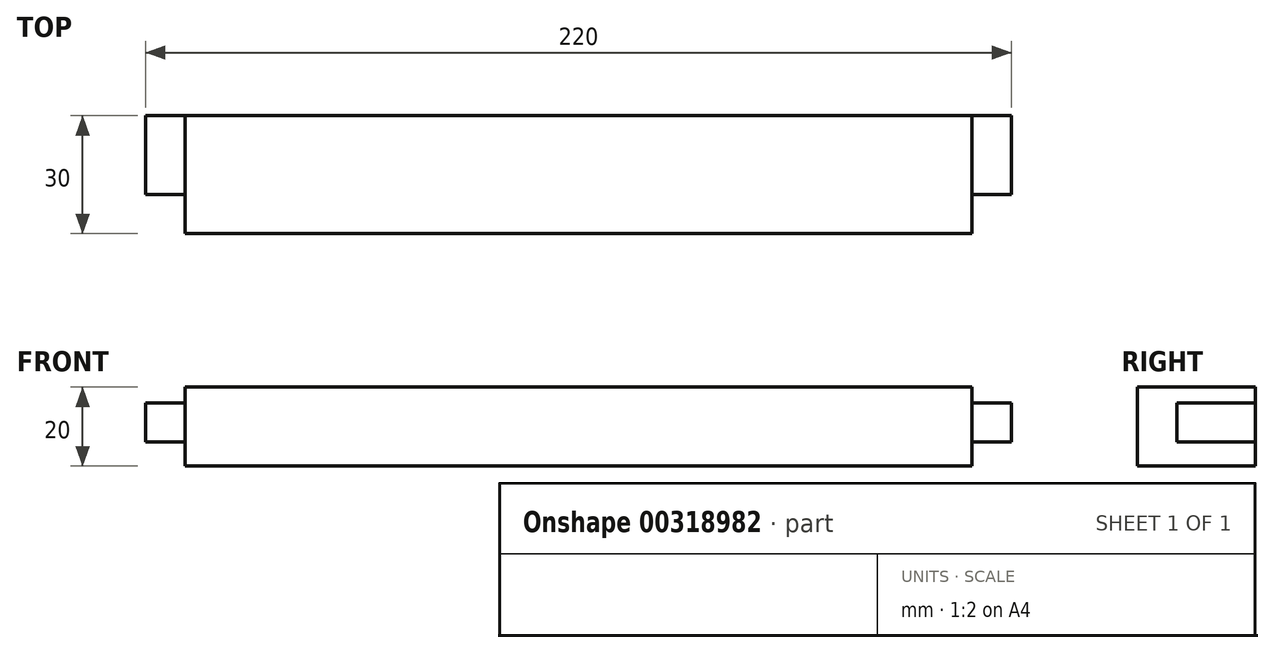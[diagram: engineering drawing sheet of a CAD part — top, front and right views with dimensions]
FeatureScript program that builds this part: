
annotation { "Feature Type Name" : "Feature", "Feature Type Description" : "" }
export const myFeature = defineFeature(function(context is Context, id is Id, definition is map)
    precondition{}
    {
        {
            var Q0;
            Q0=qCreatedBy(makeId("Top.planeOp"),FACE);
            var sketch = newSketch(context, id + "F0", { "sketchPlane" : qUnion([Q0])});
            skLineSegment(sketch, "E0.bottom", {"start": v(100, 15) * mm, "end": v(-100, 15) * mm});
            skLineSegment(sketch, "E0.top", {"start": v(100, -15) * mm, "end": v(-100, -15) * mm});
            skLineSegment(sketch, "E0.left", {"start": v(100, 15) * mm, "end": v(100, -15) * mm});
            skLineSegment(sketch, "E0.right", {"start": v(-100, 15) * mm, "end": v(-100, -15) * mm});
            skPoint(sketch, "E0.middle", {"position": v(0, 0) * mm});
            skSolve(sketch);
        }
        {
            var Q0;
            Q0=qSketchRegion(id+"F0",true);
            extrude(context, id + "F1", {"entities" : qUnion([Q0]), "depth" : 20 * mm});
        }
        {
            var Q0;
            Q0=makeQuery(id+"F1.opExtrude","SWEPT_FACE",FACE,{"disambiguationData":[OSD([sQuery(id+"F0.wireOp",EDGE,"E0.left")])]});
            var sketch = newSketch(context, id + "F2", { "sketchPlane" : qUnion([Q0])});
            skLineSegment(sketch, "E1", {"start": v(-5, 16.05) * mm, "end": v(-8.06, 20) * mm, "construction": true});
            skLineSegment(sketch, "E2.bottom", {"start": v(-5, 16.05) * mm, "end": v(15, 16.05) * mm});
            skLineSegment(sketch, "E2.top", {"start": v(-5, 6.05) * mm, "end": v(15, 6.05) * mm});
            skLineSegment(sketch, "E2.left", {"start": v(-5, 16.05) * mm, "end": v(-5, 6.05) * mm});
            skLineSegment(sketch, "E2.right", {"start": v(15, 16.05) * mm, "end": v(15, 6.05) * mm});
            skSolve(sketch);
        }
        {
            var Q0;
            Q0=qSketchRegion(id+"F2",true);
            extrude(context, id + "F3", {"entities" : qUnion([Q0]), "operationType" : NewBodyOperationType.ADD, "depth" : 10 * mm});
        }
        {
            var Q0;
            Q0=makeQuery(id+"F1.opExtrude","SWEPT_BODY",BODY,{"disambiguationData":[OSD([sQuery(id+"F0.wireOp",EDGE,"E0.bottom"),sQuery(id+"F0.wireOp",EDGE,"E0.top"),sQuery(id+"F0.wireOp",EDGE,"E0.left"),sQuery(id+"F0.wireOp",EDGE,"E0.right")])]});
            var Q1;
            Q1=qCreatedBy(makeId("Right.planeOp"),FACE);
            mirror(context, id + "F4", {"operationType" : NewBodyOperationType.ADD, "entities" : qUnion([Q0]), "mirrorPlane" : qUnion([Q1])});
        }
        {
            var Q0;
            Q0=makeQuery(id+"F1.opExtrude","SWEPT_BODY",BODY,{"disambiguationData":[OSD([sQuery(id+"F0.wireOp",EDGE,"E0.bottom"),sQuery(id+"F0.wireOp",EDGE,"E0.top"),sQuery(id+"F0.wireOp",EDGE,"E0.left"),sQuery(id+"F0.wireOp",EDGE,"E0.right")])]});
            transform(context, id + "F5", {"entities" : qUnion([Q0]), "transformType" : TransformType.TRANSLATION_3D, "dx" : 0 * mm, "dy" : 50 * mm, "dz" : 0 * mm, "makeCopy" : true});
        }
        {
            var Q0;
            Q0=makeQuery(id+"F1.opExtrude","SWEPT_BODY",BODY,{"disambiguationData":[OSD([sQuery(id+"F0.wireOp",EDGE,"E0.bottom"),sQuery(id+"F0.wireOp",EDGE,"E0.top"),sQuery(id+"F0.wireOp",EDGE,"E0.left"),sQuery(id+"F0.wireOp",EDGE,"E0.right")])]});
            deleteBodies(context, id + "F6", {"entities" : qUnion([Q0])});
        }
    });
